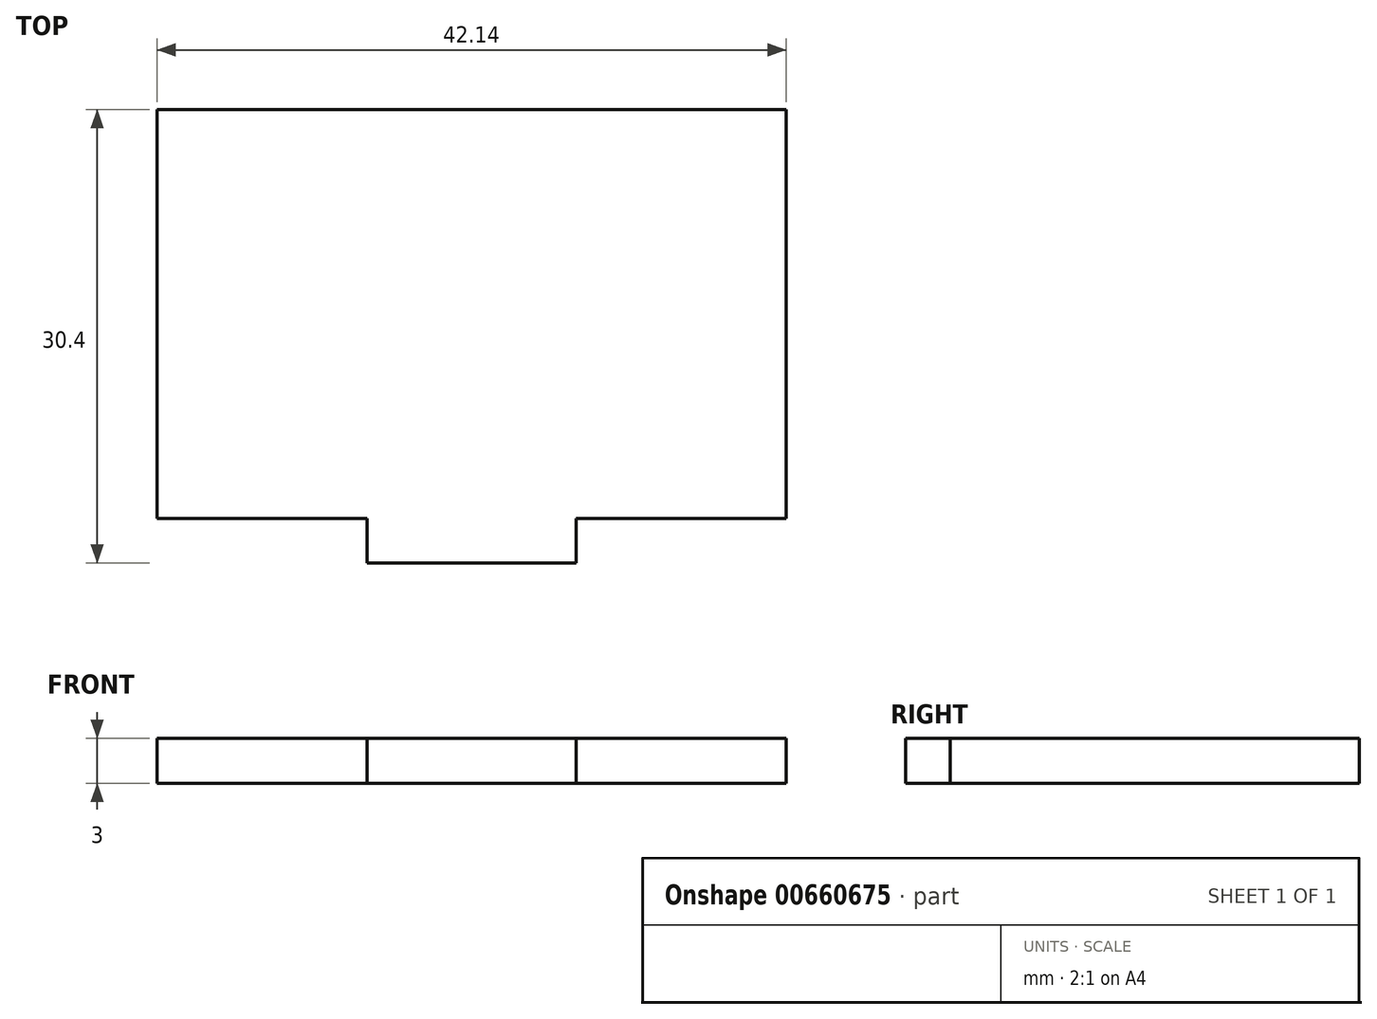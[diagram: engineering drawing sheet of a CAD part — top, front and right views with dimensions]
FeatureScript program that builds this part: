
annotation { "Feature Type Name" : "Feature", "Feature Type Description" : "" }
export const myFeature = defineFeature(function(context is Context, id is Id, definition is map)
    precondition{}
    {
        {
            var Q0;
            Q0=qCreatedBy(makeId("Top.planeOp"),FACE);
            var sketch = newSketch(context, id + "F0", { "sketchPlane" : qUnion([Q0])});
            skLineSegment(sketch, "E0.bottom", {"start": v(-21.08, 13.7) * mm, "end": v(21.08, 13.7) * mm});
            skLineSegment(sketch, "E0.top", {"start": v(-21.08, -13.7) * mm, "end": v(21.08, -13.7) * mm});
            skLineSegment(sketch, "E0.left", {"start": v(-21.07, 13.7) * mm, "end": v(-21.08, -13.7) * mm});
            skLineSegment(sketch, "E0.right", {"start": v(21.07, 13.7) * mm, "end": v(21.07, -13.7) * mm});
            skLineSegment(sketch, "E1", {"start": v(0, 13.7) * mm, "end": v(0, -13.7) * mm, "construction": true});
            skLineSegment(sketch, "E2", {"start": v(21.08, 0) * mm, "end": v(-21.08, 0) * mm, "construction": true});
            skLineSegment(sketch, "E3.bottom", {"start": v(-7, -13.7) * mm, "end": v(7, -13.7) * mm});
            skLineSegment(sketch, "E3.top", {"start": v(-7, -16.7) * mm, "end": v(7, -16.7) * mm});
            skLineSegment(sketch, "E3.left", {"start": v(-7, -13.7) * mm, "end": v(-7, -16.7) * mm});
            skLineSegment(sketch, "E3.right", {"start": v(7, -13.7) * mm, "end": v(7, -16.7) * mm});
            skLineSegment(sketch, "E4.bottom", {"start": v(0, -16.7) * mm, "end": v(0, -16.7) * mm});
            skLineSegment(sketch, "E4.top", {"start": v(0, -13.7) * mm, "end": v(0, -13.7) * mm});
            skLineSegment(sketch, "E4.left", {"start": v(0, -16.7) * mm, "end": v(0, -13.7) * mm});
            skLineSegment(sketch, "E4.right", {"start": v(0, -16.7) * mm, "end": v(0, -13.7) * mm, "construction": true});
            skSolve(sketch);
        }
        {
            var Q0;
            {var subQ0=sQuery(id+"F0.wireOp",EDGE,"E3.left");Q0=makeQuery(id+"F0.imprint","IMPRINT",FACE,{"disambiguationData":[TD([[makeQuery(id+"F0.imprint","IMPRINT",EDGE,{"derivedFrom":subQ0}),1.0]])]});}
            var Q1;
            {var subQ0=sQuery(id+"F0.wireOp",EDGE,"E3.right");Q1=makeQuery(id+"F0.imprint","IMPRINT",FACE,{"disambiguationData":[TD([[makeQuery(id+"F0.imprint","IMPRINT",EDGE,{"derivedFrom":subQ0}),-1.0]])]});}
            var Q2;
            Q2=makeQuery(id+"F0.imprint","IMPRINT",FACE,{"disambiguationData":[TD([[makeQuery(id+"F0.imprint","IMPRINT",EDGE,{"derivedFrom":sQuery(id+"F0.wireOp",EDGE,"E0.bottom")}),-1.0]])]});
            extrude(context, id + "F1", {"entities" : qUnion([Q0, Q1, Q2]), "depth" : 3 * mm, "offsetDistance" : 25 * mm});
        }
    });
